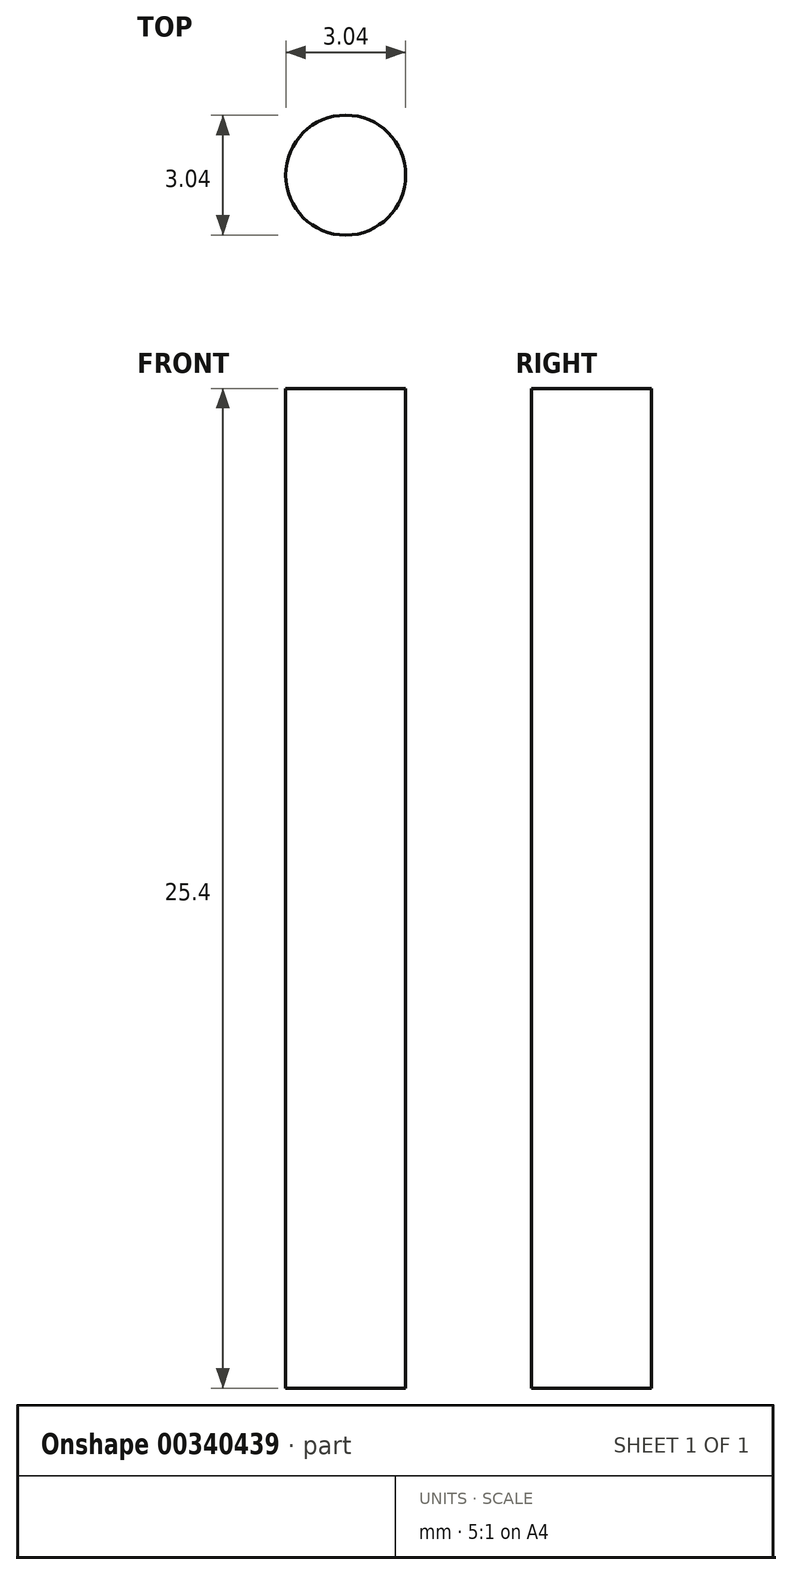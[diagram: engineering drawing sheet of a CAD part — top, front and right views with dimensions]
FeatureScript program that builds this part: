
annotation { "Feature Type Name" : "Feature", "Feature Type Description" : "" }
export const myFeature = defineFeature(function(context is Context, id is Id, definition is map)
    precondition{}
    {
        {
            var Q0;
            Q0=qCreatedBy(makeId("Top.planeOp"),FACE);
            var sketch = newSketch(context, id + "F0", { "sketchPlane" : qUnion([Q0])});
            skCircle(sketch, "E0", {"center": v(0, 0) * mm, "radius": 1.52 * mm});
            skSolve(sketch);
        }
        {
            var Q0;
            Q0 = qSketchRegion(id + "F0", true);
            extrude(context, id + "F1", {"entities" : qUnion([Q0]), "depth" : 25.4 * mm});
        }
    });
